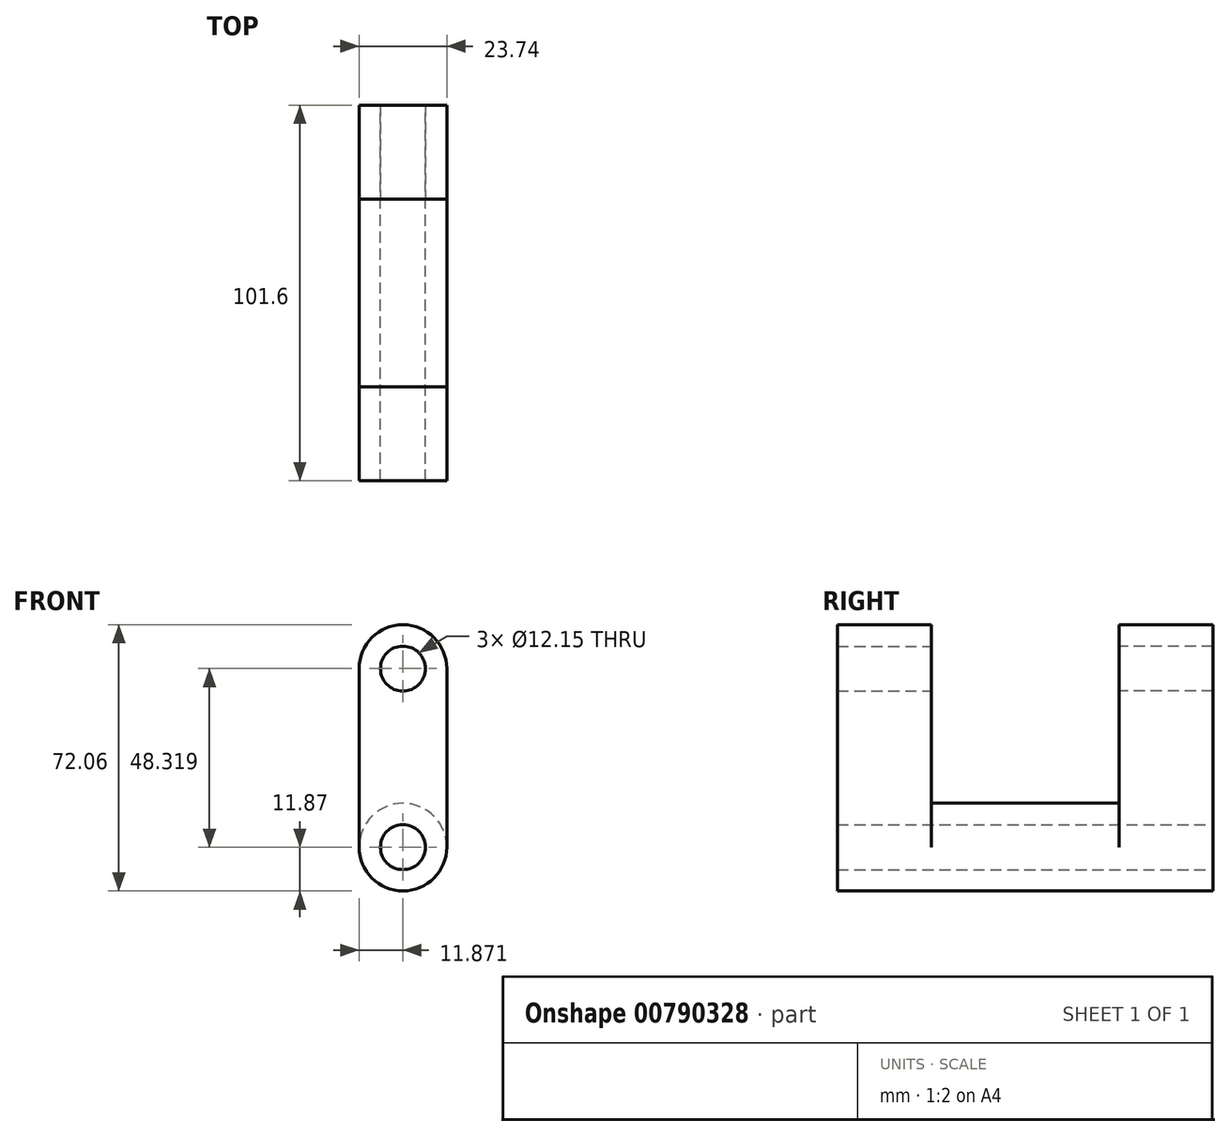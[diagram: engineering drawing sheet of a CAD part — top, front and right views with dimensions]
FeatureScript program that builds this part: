
annotation { "Feature Type Name" : "Feature", "Feature Type Description" : "" }
export const myFeature = defineFeature(function(context is Context, id is Id, definition is map)
    precondition{}
    {
        {
            var Q0;
            Q0=qCreatedBy(makeId("Front.planeOp"),FACE);
            var sketch = newSketch(context, id + "F0", { "sketchPlane" : qUnion([Q0])});
            skLineSegment(sketch, "E0", {"start": v(-23.74, 0) * mm, "end": v(-23.74, 48.32) * mm});
            skLineSegment(sketch, "E1", {"start": v(0, 48.32) * mm, "end": v(0, 0) * mm});
            skArc(sketch, "E2", {"start": v(0, 48.32) * mm, "mid": v(-11.87, 60.19) * mm, "end": v(-23.74, 48.32) * mm});
            skArc(sketch, "E3", {"start": v(-23.74, 0) * mm, "mid": v(-11.87, -11.87) * mm, "end": v(0, 0) * mm});
            skCircle(sketch, "E4", {"center": v(-11.87, 48.32) * mm, "radius": 6.08 * mm});
            skArc(sketch, "E5", {"start": v(0, 0) * mm, "mid": v(-11.87, 11.87) * mm, "end": v(-23.74, 0) * mm});
            skCircle(sketch, "E6", {"center": v(-11.87, 0) * mm, "radius": 6.08 * mm});
            skSolve(sketch);
        }
        {
            var Q0;
            Q0 = qSketchRegion(id + "F0", true);
            extrude(context, id + "F1", {"entities" : qUnion([Q0]), "depth" : 25.4 * mm, "offsetDistance" : 25.4 * mm});
        }
        {
            var Q0;
            Q0=makeQuery(id+"F0.imprint","IMPRINT",FACE,{"disambiguationData":[TD([[makeQuery(id+"F0.imprint","IMPRINT",EDGE,{"derivedFrom":sQuery(id+"F0.wireOp",EDGE,"E3")}),1.0]])]});
            extrude(context, id + "F2", {"entities" : qUnion([Q0]), "operationType" : NewBodyOperationType.ADD, "oppositeDirection" : true, "depth" : 25.4 * mm, "offsetDistance" : 25.4 * mm});
        }
        {
            var Q0;
            Q0=makeQuery(id+"F1.opExtrude","SWEPT_BODY",BODY,{"disambiguationData":[OSD([sQuery(id+"F0.wireOp",EDGE,"E0"),sQuery(id+"F0.wireOp",EDGE,"E1"),sQuery(id+"F0.wireOp",EDGE,"E2"),sQuery(id+"F0.wireOp",EDGE,"E3"),sQuery(id+"F0.wireOp",EDGE,"E4"),sQuery(id+"F0.wireOp",EDGE,"E6")])]});
            var Q1;
            Q1=makeQuery(id+"F2.opExtrude","CAP_FACE",FACE,{"disambiguationData":[OSD([sQuery(id+"F0.wireOp",EDGE,"E3"),sQuery(id+"F0.wireOp",EDGE,"E5"),sQuery(id+"F0.wireOp",EDGE,"E6")])],"isStart":false});
            mirror(context, id + "F3", {"operationType" : NewBodyOperationType.ADD, "entities" : qUnion([Q0]), "mirrorPlane" : qUnion([Q1])});
        }
    });
